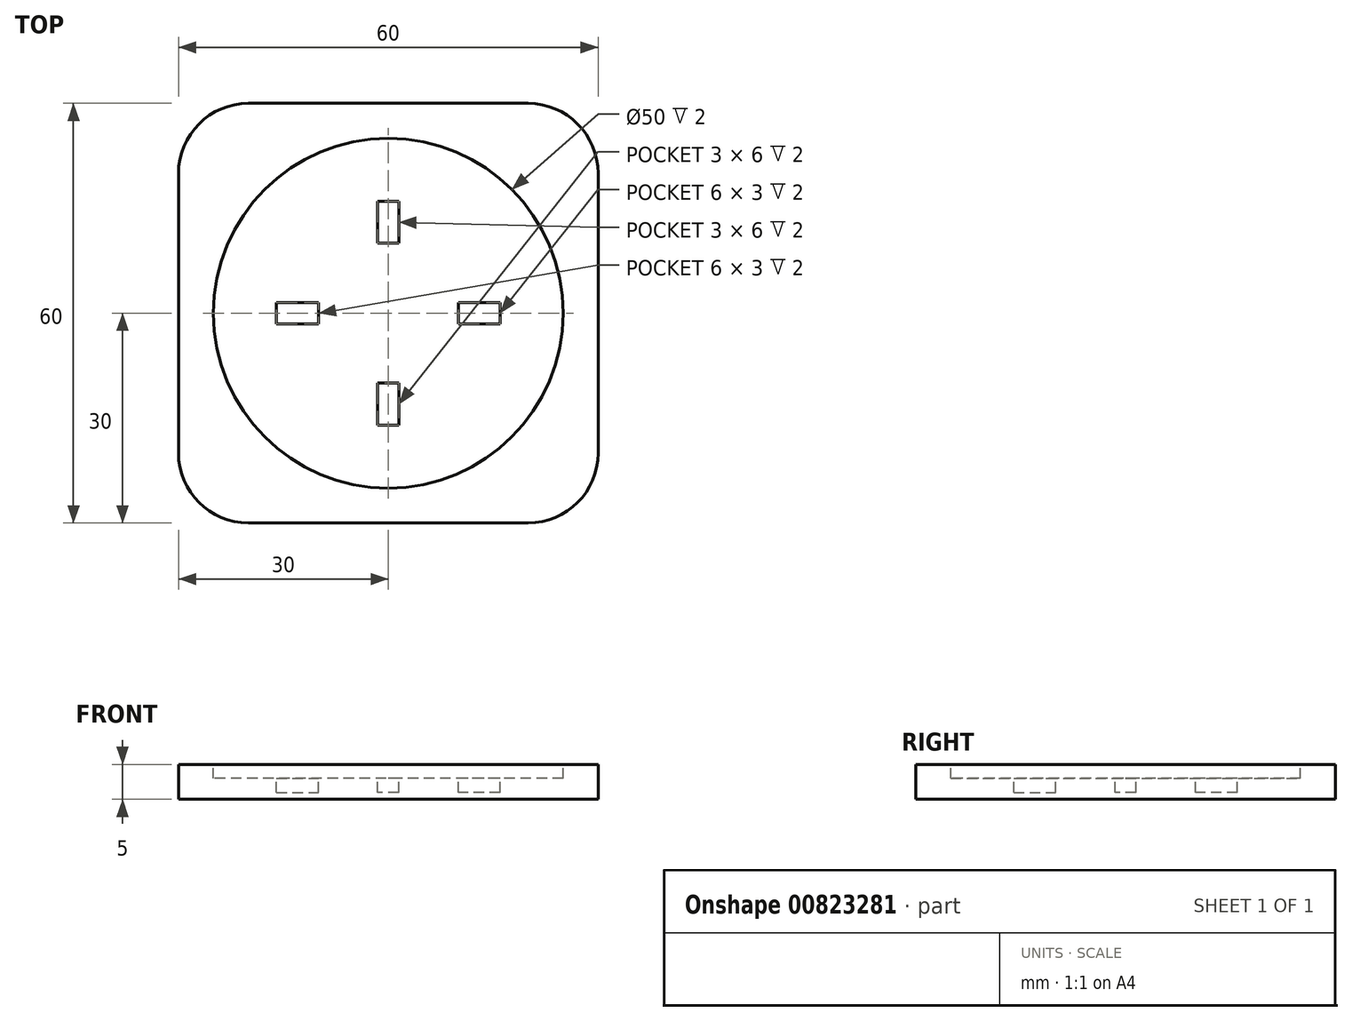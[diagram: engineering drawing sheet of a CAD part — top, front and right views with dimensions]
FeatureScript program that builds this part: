
annotation { "Feature Type Name" : "Feature", "Feature Type Description" : "" }
export const myFeature = defineFeature(function(context is Context, id is Id, definition is map)
    precondition{}
    {
        {
            var Q0;
            Q0=qCreatedBy(makeId("Top.planeOp"),FACE);
            var sketch = newSketch(context, id + "F0", { "sketchPlane" : qUnion([Q0])});
            skLineSegment(sketch, "E0.bottom", {"start": v(-30, 30) * mm, "end": v(30, 30) * mm});
            skLineSegment(sketch, "E0.top", {"start": v(-30, -30) * mm, "end": v(30, -30) * mm});
            skLineSegment(sketch, "E0.left", {"start": v(-30, 30) * mm, "end": v(-30, -30) * mm});
            skLineSegment(sketch, "E0.right", {"start": v(30, 30) * mm, "end": v(30, -30) * mm});
            skPoint(sketch, "E0.middle", {"position": v(0, 0) * mm});
            skSolve(sketch);
        }
        {
            var Q0;
            Q0=makeQuery(id+"F0.imprint","IMPRINT",FACE,{"disambiguationData":[TD([[makeQuery(id+"F0.imprint","IMPRINT",EDGE,{"derivedFrom":sQuery(id+"F0.wireOp",EDGE,"E0.bottom")}),-1.0]])]});
            extrude(context, id + "F1", {"entities" : qUnion([Q0]), "depth" : 5 * mm, "offsetDistance" : 25 * mm});
        }
        {
            var Q0;
            Q0=makeQuery(id+"F1.opExtrude","CAP_FACE",FACE,{"disambiguationData":[OSD([sQuery(id+"F0.wireOp",EDGE,"E0.bottom"),sQuery(id+"F0.wireOp",EDGE,"E0.top"),sQuery(id+"F0.wireOp",EDGE,"E0.left"),sQuery(id+"F0.wireOp",EDGE,"E0.right")])],"isStart":false});
            var sketch = newSketch(context, id + "F2", { "sketchPlane" : qUnion([Q0])});
            skCircle(sketch, "E1", {"center": v(0, 0) * mm, "radius": 25 * mm});
            skSolve(sketch);
        }
        {
            var Q0;
            Q0=makeQuery(id+"F2.imprint","IMPRINT",FACE,{"disambiguationData":[TD([[makeQuery(id+"F2.imprint","IMPRINT",EDGE,{"derivedFrom":sQuery(id+"F2.wireOp",EDGE,"E1")}),1.0]])]});
            extrude(context, id + "F3", {"entities" : qUnion([Q0]), "operationType" : NewBodyOperationType.REMOVE, "oppositeDirection" : true, "depth" : 2 * mm, "offsetDistance" : 25 * mm});
        }
        {
            var Q0;
            Q0=makeQuery(id+"F3.boolean.opBoolean","COPY",FACE,{"derivedFrom":makeQuery(id+"F3.opExtrude","CAP_FACE",FACE,{"disambiguationData":[OSD([sQuery(id+"F2.wireOp",EDGE,"E1")])],"isStart":false})});
            var sketch = newSketch(context, id + "F4", { "sketchPlane" : qUnion([Q0])});
            skLineSegment(sketch, "E2.bottom", {"start": v(-1.5, 16) * mm, "end": v(1.5, 16) * mm});
            skLineSegment(sketch, "E2.top", {"start": v(-1.5, 10) * mm, "end": v(1.5, 10) * mm});
            skLineSegment(sketch, "E2.left", {"start": v(-1.5, 16) * mm, "end": v(-1.5, 10) * mm});
            skLineSegment(sketch, "E2.right", {"start": v(1.5, 16) * mm, "end": v(1.5, 10) * mm});
            skPoint(sketch, "E2.middle", {"position": v(0, 13) * mm});
            skLineSegment(sketch, "E3.1.0", {"start": v(-16, -1.5) * mm, "end": v(-16, 1.5) * mm});
            skLineSegment(sketch, "E3.1.1", {"start": v(-10, -1.5) * mm, "end": v(-10, 1.5) * mm});
            skLineSegment(sketch, "E3.1.2", {"start": v(-16, 1.5) * mm, "end": v(-10, 1.5) * mm});
            skLineSegment(sketch, "E3.1.3", {"start": v(-16, -1.5) * mm, "end": v(-10, -1.5) * mm});
            skLineSegment(sketch, "E3.2.0", {"start": v(1.5, -16) * mm, "end": v(-1.5, -16) * mm});
            skLineSegment(sketch, "E3.2.1", {"start": v(1.5, -10) * mm, "end": v(-1.5, -10) * mm});
            skLineSegment(sketch, "E3.2.2", {"start": v(-1.5, -16) * mm, "end": v(-1.5, -10) * mm});
            skLineSegment(sketch, "E3.2.3", {"start": v(1.5, -16) * mm, "end": v(1.5, -10) * mm});
            skLineSegment(sketch, "E3.3.0", {"start": v(16, 1.5) * mm, "end": v(16, -1.5) * mm});
            skLineSegment(sketch, "E3.3.1", {"start": v(10, 1.5) * mm, "end": v(10, -1.5) * mm});
            skLineSegment(sketch, "E3.3.2", {"start": v(16, -1.5) * mm, "end": v(10, -1.5) * mm});
            skLineSegment(sketch, "E3.3.3", {"start": v(16, 1.5) * mm, "end": v(10, 1.5) * mm});
            skPoint(sketch, "E3.center", {"position": v(0, 0) * mm});
            skSolve(sketch);
        }
        {
            var Q0;
            Q0=makeQuery(id+"F4.imprint","IMPRINT",FACE,{"disambiguationData":[TD([[makeQuery(id+"F4.imprint","IMPRINT",EDGE,{"derivedFrom":sQuery(id+"F4.wireOp",EDGE,"E3.1.0")}),-1.0]])]});
            var Q1;
            Q1=makeQuery(id+"F4.imprint","IMPRINT",FACE,{"disambiguationData":[TD([[makeQuery(id+"F4.imprint","IMPRINT",EDGE,{"derivedFrom":sQuery(id+"F4.wireOp",EDGE,"E2.bottom")}),-1.0]])]});
            var Q2;
            Q2=makeQuery(id+"F4.imprint","IMPRINT",FACE,{"disambiguationData":[TD([[makeQuery(id+"F4.imprint","IMPRINT",EDGE,{"derivedFrom":sQuery(id+"F4.wireOp",EDGE,"E3.3.0")}),-1.0]])]});
            var Q3;
            Q3=makeQuery(id+"F4.imprint","IMPRINT",FACE,{"disambiguationData":[TD([[makeQuery(id+"F4.imprint","IMPRINT",EDGE,{"derivedFrom":sQuery(id+"F4.wireOp",EDGE,"E3.2.0")}),-1.0]])]});
            extrude(context, id + "F5", {"entities" : qUnion([Q0, Q1, Q2, Q3]), "operationType" : NewBodyOperationType.REMOVE, "oppositeDirection" : true, "depth" : 2 * mm, "offsetDistance" : 25 * mm});
        }
        {
            var Q0;
            Q0=makeQuery(id+"F1.opExtrude","SWEPT_EDGE",EDGE,{"disambiguationData":[OSD([sQuery(id+"F0.wireOp",EDGE,"E0.top"),sQuery(id+"F0.wireOp",EDGE,"E0.left")])]});
            var Q1;
            Q1=makeQuery(id+"F1.opExtrude","SWEPT_EDGE",EDGE,{"disambiguationData":[OSD([sQuery(id+"F0.wireOp",EDGE,"E0.bottom"),sQuery(id+"F0.wireOp",EDGE,"E0.left")])]});
            var Q2;
            Q2=makeQuery(id+"F1.opExtrude","SWEPT_EDGE",EDGE,{"disambiguationData":[OSD([sQuery(id+"F0.wireOp",EDGE,"E0.top"),sQuery(id+"F0.wireOp",EDGE,"E0.right")])]});
            var Q3;
            Q3=makeQuery(id+"F1.opExtrude","SWEPT_EDGE",EDGE,{"disambiguationData":[OSD([sQuery(id+"F0.wireOp",EDGE,"E0.bottom"),sQuery(id+"F0.wireOp",EDGE,"E0.right")])]});
            fillet(context, id + "F6", {"entities" : qUnion([Q0, Q1, Q2, Q3]), "radius" : 10 * mm, "tangentPropagation" : true, "allowEdgeOverflow" : false});
        }
    });
